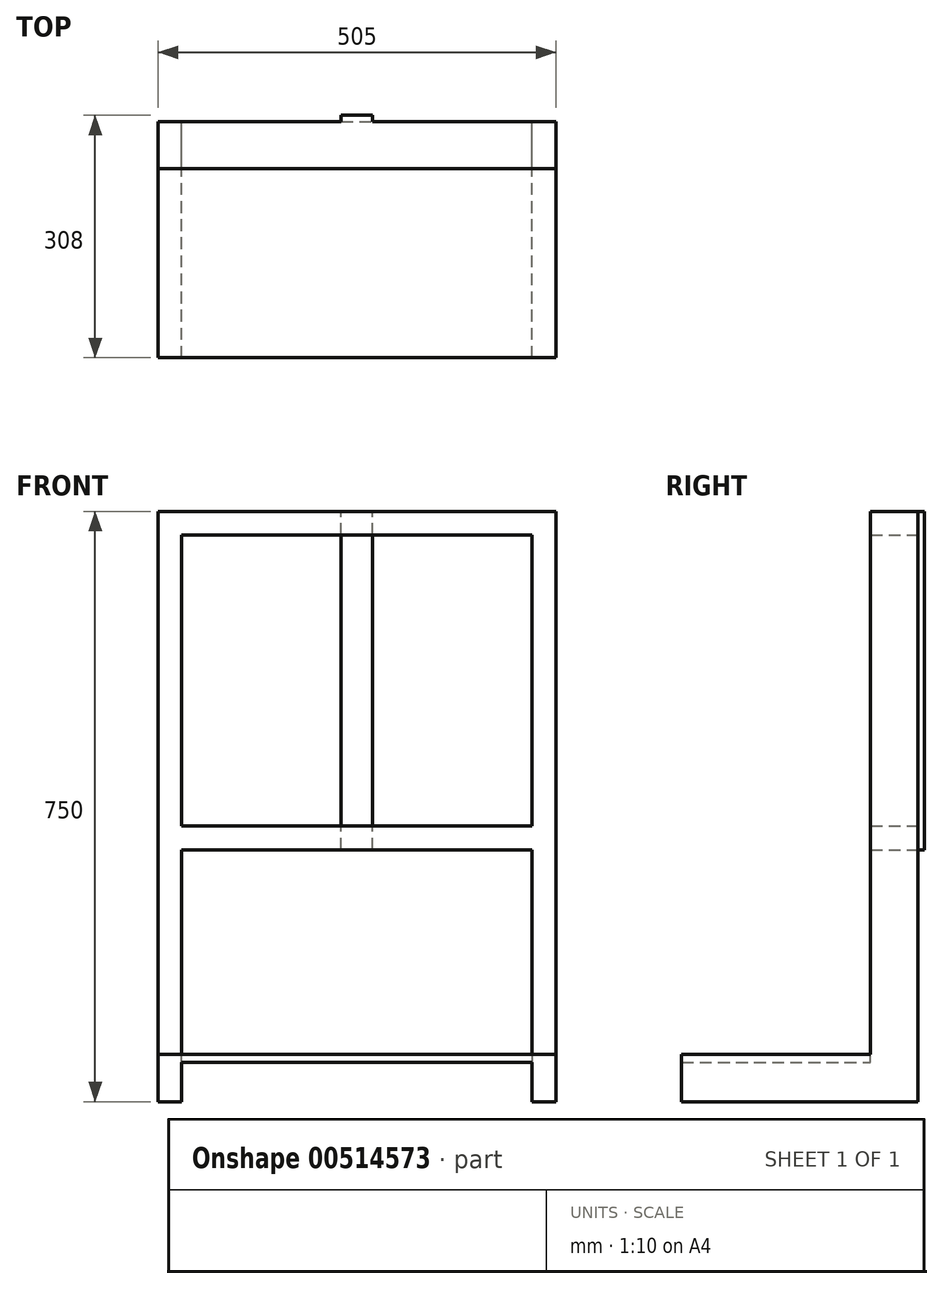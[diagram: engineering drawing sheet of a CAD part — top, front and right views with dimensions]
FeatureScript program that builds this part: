
annotation { "Feature Type Name" : "Feature", "Feature Type Description" : "" }
export const myFeature = defineFeature(function(context is Context, id is Id, definition is map)
    precondition{}
    {
        {
            var Q0;
            Q0=qCreatedBy(makeId("Front.planeOp"),FACE);
            var sketch = newSketch(context, id + "F0", { "sketchPlane" : qUnion([Q0])});
            skLineSegment(sketch, "E0.bottom", {"start": v(0, 750) * mm, "end": v(505, 750) * mm});
            skLineSegment(sketch, "E0.top", {"start": v(0, 0) * mm, "end": v(30, 0) * mm});
            skLineSegment(sketch, "E0.left", {"start": v(0, 750) * mm, "end": v(0, 0) * mm});
            skLineSegment(sketch, "E0.right", {"start": v(505, 750) * mm, "end": v(505, 0) * mm});
            skLineSegment(sketch, "E1.bottom", {"start": v(30, 720) * mm, "end": v(475, 720) * mm});
            skLineSegment(sketch, "E1.left", {"start": v(30, 720) * mm, "end": v(30, 350) * mm});
            skLineSegment(sketch, "E1.right", {"start": v(475, 720) * mm, "end": v(475, 350) * mm});
            skLineSegment(sketch, "E2.bottom", {"start": v(30, 350) * mm, "end": v(475, 350) * mm});
            skLineSegment(sketch, "E2.top", {"start": v(30, 320) * mm, "end": v(475, 320) * mm});
            skLineSegment(sketch, "E3.trimOffspring", {"start": v(30, 320) * mm, "end": v(30, 0) * mm});
            skLineSegment(sketch, "E4.trimOffspring", {"start": v(475, 320) * mm, "end": v(475, 0) * mm});
            skLineSegment(sketch, "E5.trimOffspring", {"start": v(475, 0) * mm, "end": v(505, 0) * mm});
            skSolve(sketch);
        }
        {
            var Q0;
            Q0 = qSketchRegion(id + "F0", true);
            extrude(context, id + "F1", {"entities" : qUnion([Q0]), "depth" : 60 * mm, "offsetDistance" : 25 * mm});
        }
        {
            var Q0;
            Q0=makeQuery(id+"F1.opExtrude","CAP_FACE",FACE,{"disambiguationData":[OSD([sQuery(id+"F0.wireOp",EDGE,"E0.bottom"),sQuery(id+"F0.wireOp",EDGE,"E0.top"),sQuery(id+"F0.wireOp",EDGE,"E0.left"),sQuery(id+"F0.wireOp",EDGE,"E0.right"),sQuery(id+"F0.wireOp",EDGE,"E1.bottom"),sQuery(id+"F0.wireOp",EDGE,"E1.left"),sQuery(id+"F0.wireOp",EDGE,"E1.right"),sQuery(id+"F0.wireOp",EDGE,"E2.bottom"),sQuery(id+"F0.wireOp",EDGE,"E2.top"),sQuery(id+"F0.wireOp",EDGE,"E3.trimOffspring"),sQuery(id+"F0.wireOp",EDGE,"E4.trimOffspring"),sQuery(id+"F0.wireOp",EDGE,"E5.trimOffspring")])],"isStart":false});
            var sketch = newSketch(context, id + "F2", { "sketchPlane" : qUnion([Q0])});
            skLineSegment(sketch, "E6.bottom", {"start": v(0, 0) * mm, "end": v(30, 0) * mm});
            skLineSegment(sketch, "E6.top", {"start": v(0, 50) * mm, "end": v(30, 50) * mm});
            skLineSegment(sketch, "E6.left", {"start": v(0, 0) * mm, "end": v(0, 50) * mm});
            skLineSegment(sketch, "E6.right", {"start": v(30, 0) * mm, "end": v(30, 50) * mm});
            skLineSegment(sketch, "E7.bottom", {"start": v(475, 0) * mm, "end": v(505, 0) * mm});
            skLineSegment(sketch, "E7.top", {"start": v(475, 50) * mm, "end": v(505, 50) * mm});
            skLineSegment(sketch, "E7.left", {"start": v(475, 0) * mm, "end": v(475, 50) * mm});
            skLineSegment(sketch, "E7.right", {"start": v(505, 0) * mm, "end": v(505, 50) * mm});
            skSolve(sketch);
        }
        {
            var Q0;
            Q0 = qSketchRegion(id + "F2", true);
            extrude(context, id + "F3", {"entities" : qUnion([Q0]), "operationType" : NewBodyOperationType.ADD, "depth" : 240 * mm, "offsetDistance" : 25 * mm});
        }
        {
            var Q0;
            Q0=makeQuery(id+"F3.opExtrude","SWEPT_FACE",FACE,{"disambiguationData":[OSD([sQuery(id+"F2.wireOp",EDGE,"E6.top")])]});
            var sketch = newSketch(context, id + "F4", { "sketchPlane" : qUnion([Q0])});
            skLineSegment(sketch, "E8.bottom", {"start": v(0, -60) * mm, "end": v(505, -60) * mm});
            skLineSegment(sketch, "E8.top", {"start": v(0, -300) * mm, "end": v(505, -300) * mm});
            skLineSegment(sketch, "E8.left", {"start": v(0, -60) * mm, "end": v(0, -300) * mm});
            skLineSegment(sketch, "E8.right", {"start": v(505, -60) * mm, "end": v(505, -300) * mm});
            skSolve(sketch);
        }
        {
            var Q0;
            Q0 = qSketchRegion(id + "F4", true);
            extrude(context, id + "F5", {"entities" : qUnion([Q0]), "operationType" : NewBodyOperationType.ADD, "depth" : 10 * mm, "offsetDistance" : 25 * mm});
        }
        {
            var Q0;
            Q0=makeQuery(id+"F1.opExtrude","CAP_FACE",FACE,{"disambiguationData":[OSD([sQuery(id+"F0.wireOp",EDGE,"E0.bottom"),sQuery(id+"F0.wireOp",EDGE,"E0.top"),sQuery(id+"F0.wireOp",EDGE,"E0.left"),sQuery(id+"F0.wireOp",EDGE,"E0.right"),sQuery(id+"F0.wireOp",EDGE,"E1.bottom"),sQuery(id+"F0.wireOp",EDGE,"E1.left"),sQuery(id+"F0.wireOp",EDGE,"E1.right"),sQuery(id+"F0.wireOp",EDGE,"E2.bottom"),sQuery(id+"F0.wireOp",EDGE,"E2.top"),sQuery(id+"F0.wireOp",EDGE,"E3.trimOffspring"),sQuery(id+"F0.wireOp",EDGE,"E4.trimOffspring"),sQuery(id+"F0.wireOp",EDGE,"E5.trimOffspring")])],"isStart":true});
            var sketch = newSketch(context, id + "F6", { "sketchPlane" : qUnion([Q0])});
            skLineSegment(sketch, "E9.bottom", {"start": v(-272.5, 320) * mm, "end": v(-232.5, 320) * mm});
            skLineSegment(sketch, "E9.top", {"start": v(-272.5, 750) * mm, "end": v(-232.5, 750) * mm});
            skLineSegment(sketch, "E9.left", {"start": v(-272.5, 320) * mm, "end": v(-272.5, 750) * mm});
            skLineSegment(sketch, "E9.right", {"start": v(-232.5, 320) * mm, "end": v(-232.5, 750) * mm});
            skSolve(sketch);
        }
        {
            var Q0;
            Q0 = qSketchRegion(id + "F6", true);
            extrude(context, id + "F7", {"entities" : qUnion([Q0]), "operationType" : NewBodyOperationType.ADD, "depth" : 8 * mm, "offsetDistance" : 25 * mm});
        }
    });
